FCSTD DOCUMENT  (FreeCAD 0.21R33771 (Git))
Label: ViteRicircolo12x350
License: All rights reserved
LicenseURL: http://en.wikipedia.org/wiki/All_rights_reserved
objects: Sketcher::SketchObject×1, PartDesign::CoordinateSystem×1, PartDesign::Body×1
note: 3 computed .brp shape members not serialized (recipe doc carries the construction recipe); baked Part::Feature solids carry a one-line shape summary decoded from their .brp

FEATURE [Sketcher::SketchObject] Sketch
  FullyConstrained = true
  MapMode = 5
  Support = -> [XY_Plane]
  sketch-geometry (10):
    g0: LineSegment StartX=0 StartY=0 StartZ=0 EndX=0 EndY=4 EndZ=0
    g1: LineSegment StartX=0 StartY=4 StartZ=0 EndX=15 EndY=4 EndZ=0
    g2: LineSegment StartX=15 StartY=4 StartZ=0 EndX=15 EndY=5 EndZ=0
    g3: LineSegment StartX=15 StartY=5 StartZ=0 EndX=54 EndY=5 EndZ=0
    g4: LineSegment StartX=54 StartY=5 StartZ=0 EndX=54 EndY=6 EndZ=0
    g5: LineSegment StartX=54 StartY=6 StartZ=0 EndX=340 EndY=6 EndZ=0
    g6: LineSegment StartX=340 StartY=6 StartZ=0 EndX=340 EndY=4 EndZ=0
    g7: LineSegment StartX=340 StartY=4 StartZ=0 EndX=350 EndY=4 EndZ=0
    g8: LineSegment StartX=350 StartY=4 StartZ=0 EndX=350 EndY=0 EndZ=0
    g9: LineSegment StartX=350 StartY=0 StartZ=0 EndX=0 EndY=0 EndZ=0
  constraints (29):
    c: Coincident(g0,g-1)
    c: PointOnObject(g0,g-2)
    c: Coincident(g1,g0)
    c: Horizontal(g1)
    c: Coincident(g2,g1)
    c: Vertical(g2)
    c: Coincident(g3,g2)
    c: Horizontal(g3)
    c: Coincident(g4,g3)
    c: Vertical(g4)
    c: Coincident(g5,g4)
    c: Horizontal(g5)
    c: Coincident(g6,g5)
    c: Vertical(g6)
    c: Coincident(g7,g6)
    c: Horizontal(g7)
    c: Coincident(g8,g7)
    c: PointOnObject(g8,g-1)
    c: Vertical(g8)
    c: Coincident(g9,g8)
    c: Coincident(g9,g0)
    c: DistanceX(g1,g1) = 15
    c: DistanceX(g3,g3) = 39
    c: DistanceX(g7,g7) = 10
    c: DistanceX(g0,g7) = 350
    c: DistanceY(g0,g0) = 4
    c: DistanceY(g2,g2) = 1
    c: DistanceY(g4,g4) = 1
    c: DistanceY(g8,g8) = 4
FEATURE [PartDesign::CoordinateSystem] LCS_ViteRicircolo12x350
  AttacherType = Attacher::AttachEngine3D
FEATURE [PartDesign::Body] Body  label="Corpo"
  Group = -> [Sketch,LCS_ViteRicircolo12x350]
  Origin = -> Origin
